# Revit family: IS_ConnectSpace_E1185_BIM_IT
name_source: partatom
category: Plumbing Fixtures
revit_build: Autodesk Revit MEP 2016 (Build: 20161004_0715(x64)
units: mm (PartAtom-declared; Revit-internal decimal feet)

## family parameters
Always vertical = No
Cut with Voids When Loaded = No
OmniClass Number = 23.45.05.21.11.11
OmniClass Title = Water Operated Water Closets
Part Type = Normal
Room Calculation Point = No
Round Connector Dimension = Use Diameter
Shared = No
Work Plane-Based = No

## types (1)
- E118501 - CNCT SPACE VASO X CASSETTA SC.ORIZZ.BEU
    Accessori = www.idealstandard.it
    AltezzaNominale = 400 mm
    Assembly Code = C1030200
    BIMobject category = Toilets
    BOSUseNativeGeometries = 1
    Brand = Ideal Standard
    Brand url = http://www.idealstandard.co.uk
    Caratteristiche = Vaso per cassetta Connect Space scarico a parete a profondità ridotta a soli 60 cm. Il vaso è corredato di fissaggi a pavimento. La cassetta e il sedile sono disponibili a richiesta. Cassetta angolare in foto. Vaso per cassetta scarico orizzontale.
    CodiceABarre = 5017830447924
    CodiceArticolo = E118501
    CodiceRiferimento = CNCT SPACE VASO X CASSETTA SC.ORIZZ.BEU
    Colore = Bianco
    Connessione = Installazione
    CostoDiSostituzione = 0 $
    Description = CNCT SPACE VASO X CASSETTA SC.ORIZZ.BEU
    Dimensione = 360x600x400 mm
    DurataGaranzia = 99
    DurataGaranziaProdotti = 99
    EAN code = https://5017830447924
    Edition number = 1
    Finitura = Bianco
    Forma = Scultura
    Garanzia = Garanzia Idealstandard
    IFC Classification = Sanitary Terminal
    InformaziniGaranzia = www.idealstandard.it/garanzia.html
    InformazioniGaranzia = www.idealstandard.it/garanzia.html
    Installation instructions = http://www.idealstandard.it
    InstruzioniInstallazione = www.idealstandard.it/prodotti/html
    LarghezzaNominale = 361 mm
    LunghezzaNominale = 600 mm
    Manufacturer name = Ideal Standard
    Material main = Ceramics
    Materiale = Porcellana Vetrificata (Vitreous China)
    Model = E118501
    NBS Reference Code = 35-93-94
    NBS Reference Description = Wc Pans
    Nome = CNCT SPACE VASO X CASSETTA SC.ORIZZ.BEU
    Nominal height = 775
    Nominal width = 365
    NumeroDiModello = E118501
    OmniClass Code = 23-31 19 00
    OmniClass Description = Toilets
    PesoNetto = 24,53 KG
    Product Guid = 98935c44-42dc-4462-8e69-a0fd4bc7169f
    Product SKU = E1185
    Product certification = http://www.idealstandard.it
    Product data url = https://bimobject.com
    Product family = CONNECT SPACE
    Product group = Bowl
    Product name = CONNECT SPACE CLOSE COUPLED BOWL HO WHITE
    Product url = http://www.idealstandard.it
    QR code = http://bimobject.com
    Spazio = Interno
    Technical description = http://www.idealstandard.it
    Telefono = 800 652 290
    TipoDiDato = Fisso
    TipologiaVaso = Altro
    URL = www.idealstandard.it
    Uniclass 1.4 Code = L7216
    Uniclass 1.4 Description = Toilets
    Uniclass 2.0 Code = PR-35-93-94
    Uniclass 2.0 Description = Wc Pans
    Uniclass 2015 Code = Pr_40_20_93_94
    Uniclass 2015 Name = WC pans
    UnitaDurata = anni
    UnitaDurataGaranzia = anni
    UnitaLineare = millimetri
    UnitaSuperficie = millimetri
    UnitaVolume = Litri
    Versione = 1
    Weight Net (Kg) = 24.53
    Youtube clip = http://www.idealstandard.it

## geometry (parser evidence)
native form markers: Blend x4, Sweep x1
no freeform markers — native parametric forms only
